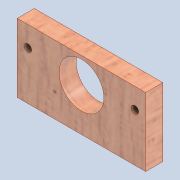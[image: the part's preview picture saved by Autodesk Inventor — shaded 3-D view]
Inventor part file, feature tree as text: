
AUTODESK INVENTOR PART (.ipt)
format: ipt  version: 2020 (Build 240168000, 168)  size: 257,536 bytes
history: native  units: mm
features: extrude x3, sketch x3, direct_edit x1, move_body x1
ambient origin geometry x8: Origin, YZ Plane, XZ Plane, XY Plane, X Axis, Y Axis, Z Axis, Center Point
bodies: Solid1 (feature_tree)
feature tree (8):
  extrude  "Extrusion1"  Depth=60.0mm
  extrude  "Extrusion2"  Depth=8.0mm
  extrude  "Extrusion3"  TaperAngle=0.0deg  [1 undecoded]
  direct_edit  "Direct Edit1"
  sketch  "Sketch1"  dims[d0=60.0mm d1=35.0mm]
  sketch  "Sketch2"  dims[d2=8.0mm d3=0.0mm d4=5.0mm]
  sketch  "Sketch3"  dims[d5=21.0mm d6=0.0mm d7=0.0mm d9=3.5mm d10=3.5mm d11=10.0mm d12=2.5mm d13=5.0mm d14=5.0mm d15=0.0mm d16=0.0mm d17=21.0mm d18=15.0mm d19=0.0mm d20=0.0mm d21=-3.0mm]
  move_body  "Move1"
note: 1 required parameter value undecoded (feature->parameter linkage not recoverable at this tier; creation-order binding heuristic only, values carry confidence <= 0.55)
